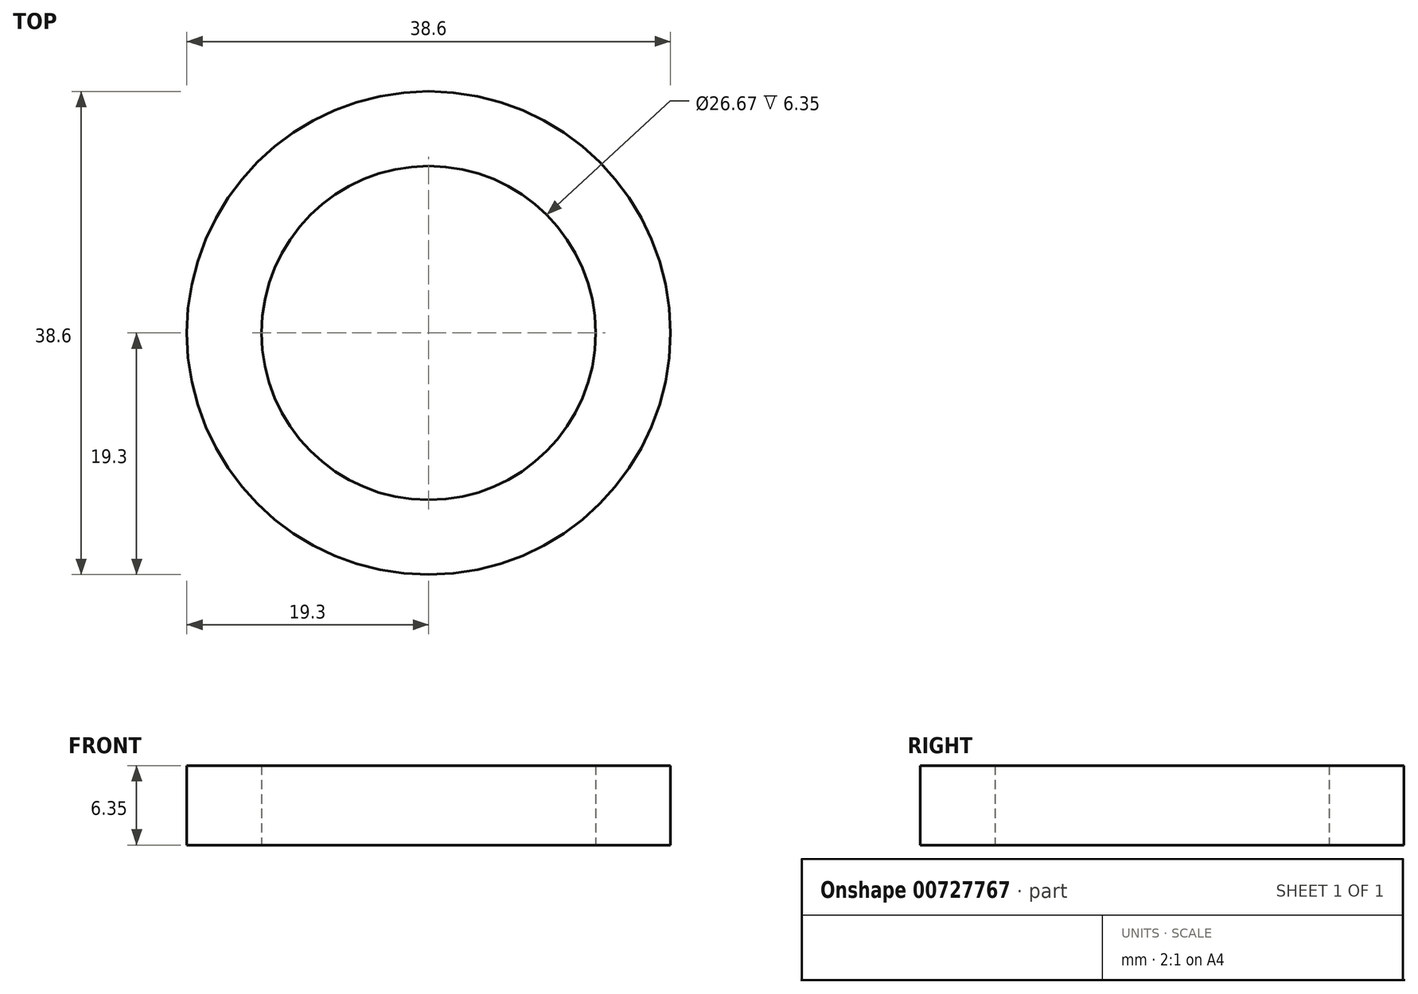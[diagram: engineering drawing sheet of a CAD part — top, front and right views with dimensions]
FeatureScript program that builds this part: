
annotation { "Feature Type Name" : "Feature", "Feature Type Description" : "" }
export const myFeature = defineFeature(function(context is Context, id is Id, definition is map)
    precondition{}
    {
        {
            var Q0;
            Q0=qCreatedBy(makeId("Top.planeOp"),FACE);
            var sketch = newSketch(context, id + "F0", { "sketchPlane" : qUnion([Q0])});
            skCircle(sketch, "E0", {"center": v(0, 0) * mm, "radius": 19.3 * mm});
            skCircle(sketch, "E1", {"center": v(0, 0) * mm, "radius": 13.34 * mm});
            skSolve(sketch);
        }
        {
            var Q0;
            Q0 = qSketchRegion(id + "F0", true);
            extrude(context, id + "F1", {"entities" : qUnion([Q0]), "depth" : 6.35 * mm, "offsetDistance" : 25.4 * mm});
        }
    });
